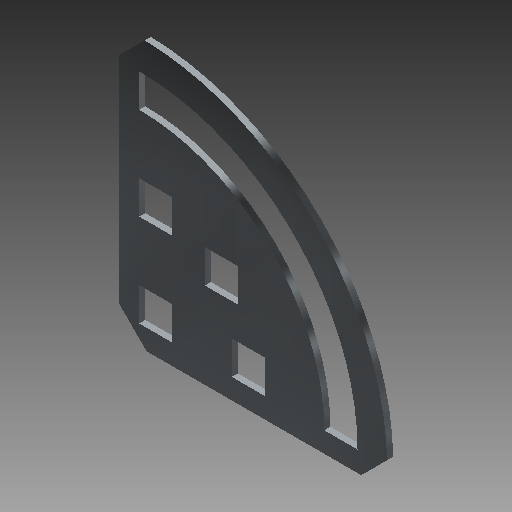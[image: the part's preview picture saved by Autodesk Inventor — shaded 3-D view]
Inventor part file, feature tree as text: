
AUTODESK INVENTOR PART (.ipt)
format: ipt  version: 2018 (Build 220112000, 112)  size: 194,048 bytes
history: native  units: mm (DEFAULTED — no unit token found)
features: extrude x7, other x6, sketch x5, pattern_linear x2
ambient origin geometry x8: Origin, YZ Plane, XZ Plane, XY Plane, X Axis, Y Axis, Z Axis, Center Point
bodies: Solid1 (feature_tree)
feature tree (20):
  extrude  "Extrusion1"  Depth=4.572mm
  pattern_linear  "Rectangular Pattern1"  Spacing1=8.128mm  [1 undecoded]
  pattern_linear  "Rectangular Pattern2"  Spacing1=8.128mm  [1 undecoded]
  sketch  "Sketch1"  dims[d0=4.572mm d1=4.572mm]
  sketch  "Sketch2"  dims[d2=4.572mm]
  other  "Srf1"
  other  "Srf2"
  other  "Srf3"
  sketch  "Sketch3"  dims[d3=4.572mm]
  other  "Srf4"
  sketch  "Sketch4"  dims[d4=4.572mm]
  other  "Srf5"
  sketch  "Sketch5"  dims[d5=4.572mm d6=8.128mm d8=8.128mm d10=4.064mm d11=2.794mm d12=2.794mm d13=3.81mm d14=3.81mm d15=3.81mm d16=3.81mm d18=45.0deg d22=4.572mm d23=4.445mm d24=4.445mm d25=4.572mm d26=0.8382mm d27=0.0mm d28=25.4mm d29=0.0mm d30=20.0mm d32=12.7mm d33=20.0mm d35=12.7mm d36=25.4mm d37=0.0mm d38=0.0mm d39=0.0mm d40=0.0mm d41=0.0mm d42=0.0mm d43=0.0mm d44=0.0mm d45=0.0mm d46=25.4mm d47=0.0mm d48=25.4mm d49=0.0mm d50=0.0mm d51=0.0mm d52=0.0mm d53=0.0mm]
  other  "Srf6"
  extrude  "ExtrusionSrf1"  Depth=25.4mm
  extrude  "ExtrusionSrf4"  Depth=2.794mm
  extrude  "ExtrusionSrf5"  Depth=2.794mm
  extrude  "ExtrusionSrf6"  Depth=25.4mm
  extrude  "ExtrusionSrf2"  Depth=25.4mm
  extrude  "ExtrusionSrf3"  Depth=25.4mm
note: 2 required parameter values undecoded (feature->parameter linkage not recoverable at this tier; creation-order binding heuristic only, values carry confidence <= 0.55)
